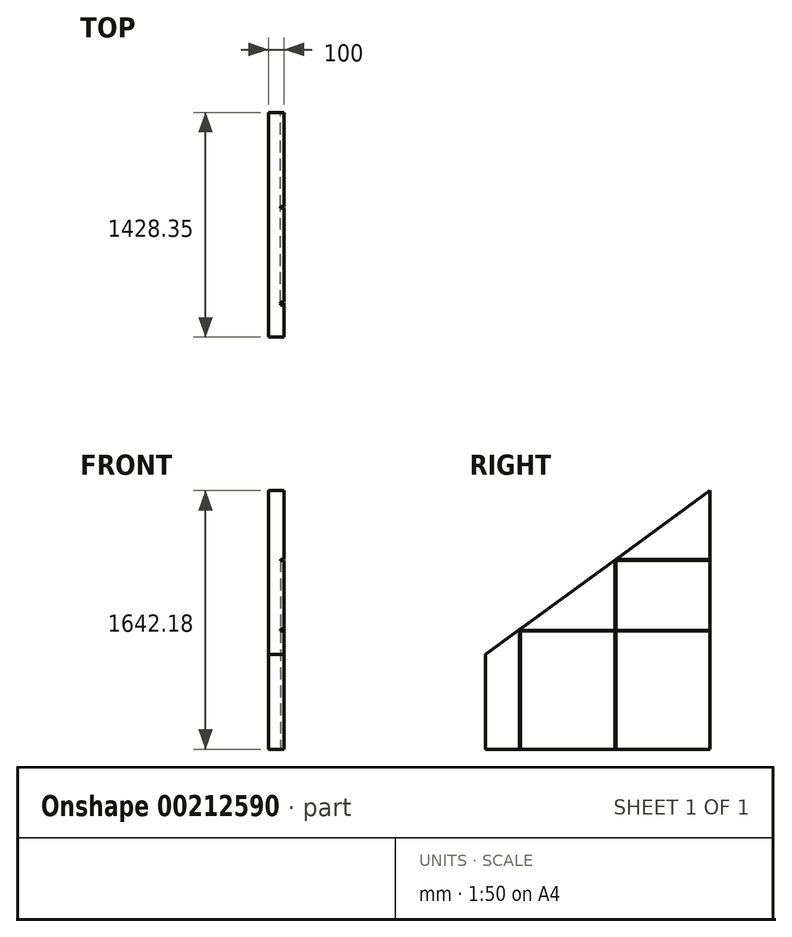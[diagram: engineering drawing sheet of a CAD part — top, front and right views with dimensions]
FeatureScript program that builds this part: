
annotation { "Feature Type Name" : "Feature", "Feature Type Description" : "" }
export const myFeature = defineFeature(function(context is Context, id is Id, definition is map)
    precondition{}
    {
        {
            var Q0;
            Q0=qCreatedBy(makeId("Right.planeOp"),FACE);
            var sketch = newSketch(context, id + "F0", { "sketchPlane" : qUnion([Q0])});
            skLineSegment(sketch, "E0", {"start": v(299.03, 33.49) * mm, "end": v(2949.03, 33.49) * mm, "construction": true});
            skLineSegment(sketch, "E1", {"start": v(2949.03, 33.49) * mm, "end": v(2949.03, 1819.49) * mm, "construction": true});
            skLineSegment(sketch, "E2", {"start": v(2949.03, 1819.49) * mm, "end": v(1899.03, 1819.49) * mm, "construction": true});
            skLineSegment(sketch, "E3", {"start": v(1899.03, 1819.49) * mm, "end": v(299.03, 653.49) * mm, "construction": true});
            skLineSegment(sketch, "E4", {"start": v(299.03, 653.49) * mm, "end": v(299.03, 33.49) * mm, "construction": true});
            skLineSegment(sketch, "E5", {"start": v(389.03, 33.49) * mm, "end": v(389.03, 634.76) * mm});
            skLineSegment(sketch, "E6", {"start": v(389.03, 634.76) * mm, "end": v(1817.38, 1675.67) * mm});
            skLineSegment(sketch, "E7", {"start": v(1817.38, 1675.67) * mm, "end": v(1817.38, 33.49) * mm});
            skLineSegment(sketch, "E8", {"start": v(1817.38, 33.49) * mm, "end": v(389.03, 33.49) * mm});
            skSolve(sketch);
        }
        {
            var Q0;
            Q0=makeQuery(id+"F0.imprint","IMPRINT",FACE,{"disambiguationData":[TD([[makeQuery(id+"F0.imprint","IMPRINT",EDGE,{"derivedFrom":sQuery(id+"F0.wireOp",EDGE,"E5")}),-1.0]])]});
            extrude(context, id + "F1", {"entities" : qUnion([Q0]), "oppositeDirection" : true, "depth" : 100 * mm});
        }
        {
            var Q0;
            Q0=qCreatedBy(makeId("Right.planeOp"),FACE);
            var sketch = newSketch(context, id + "F2", { "sketchPlane" : qUnion([Q0])});
            skLineSegment(sketch, "E9.bottom", {"start": v(1217.38, 1819.49) * mm, "end": v(1212.38, 1819.49) * mm});
            skLineSegment(sketch, "E9.top", {"start": v(1217.38, 33.49) * mm, "end": v(1212.38, 33.49) * mm});
            skLineSegment(sketch, "E9.left", {"start": v(1217.38, 1819.49) * mm, "end": v(1217.38, 33.49) * mm});
            skLineSegment(sketch, "E9.right", {"start": v(1212.38, 1819.49) * mm, "end": v(1212.38, 33.49) * mm});
            skLineSegment(sketch, "E10.bottom", {"start": v(612.38, 1819.49) * mm, "end": v(607.38, 1819.49) * mm});
            skLineSegment(sketch, "E10.top", {"start": v(612.38, 33.49) * mm, "end": v(607.38, 33.49) * mm});
            skLineSegment(sketch, "E10.left", {"start": v(612.38, 1819.49) * mm, "end": v(612.38, 33.49) * mm});
            skLineSegment(sketch, "E10.right", {"start": v(607.38, 1819.49) * mm, "end": v(607.38, 33.49) * mm});
            skLineSegment(sketch, "E11.bottom", {"start": v(0, 1238.49) * mm, "end": v(2854.16, 1238.49) * mm});
            skLineSegment(sketch, "E11.top", {"start": v(0, 1233.49) * mm, "end": v(2854.16, 1233.49) * mm});
            skLineSegment(sketch, "E11.left", {"start": v(0, 1238.49) * mm, "end": v(0, 1233.49) * mm});
            skLineSegment(sketch, "E11.right", {"start": v(2854.16, 1238.49) * mm, "end": v(2854.16, 1233.49) * mm});
            skSolve(sketch);
        }
        {
            var Q0;
            Q0=qSketchRegion(id+"F2",true);
            extrude(context, id + "F3", {"entities" : qUnion([Q0]), "operationType" : NewBodyOperationType.REMOVE, "oppositeDirection" : true, "depth" : 25 * mm});
        }
        {
            var Q0;
            Q0=makeQuery(id+"F0.imprint","IMPRINT",FACE,{"disambiguationData":[TD([[makeQuery(id+"F0.imprint","IMPRINT",EDGE,{"derivedFrom":sQuery(id+"F0.wireOp",EDGE,"E5")}),-1.0]])]});
            var sketch = newSketch(context, id + "F4", { "sketchPlane" : qUnion([Q0])});
            skLineSegment(sketch, "E12.bottom", {"start": v(299.03, 788.49) * mm, "end": v(2949.03, 788.49) * mm});
            skLineSegment(sketch, "E12.top", {"start": v(299.03, 783.49) * mm, "end": v(2949.03, 783.49) * mm});
            skLineSegment(sketch, "E12.left", {"start": v(299.03, 788.49) * mm, "end": v(299.03, 783.49) * mm});
            skLineSegment(sketch, "E12.right", {"start": v(2949.03, 788.49) * mm, "end": v(2949.03, 783.49) * mm});
            skSolve(sketch);
        }
        {
            var Q0;
            Q0=qSketchRegion(id+"F4",true);
            extrude(context, id + "F5", {"entities" : qUnion([Q0]), "operationType" : NewBodyOperationType.REMOVE, "oppositeDirection" : true, "depth" : 25 * mm});
        }
    });
